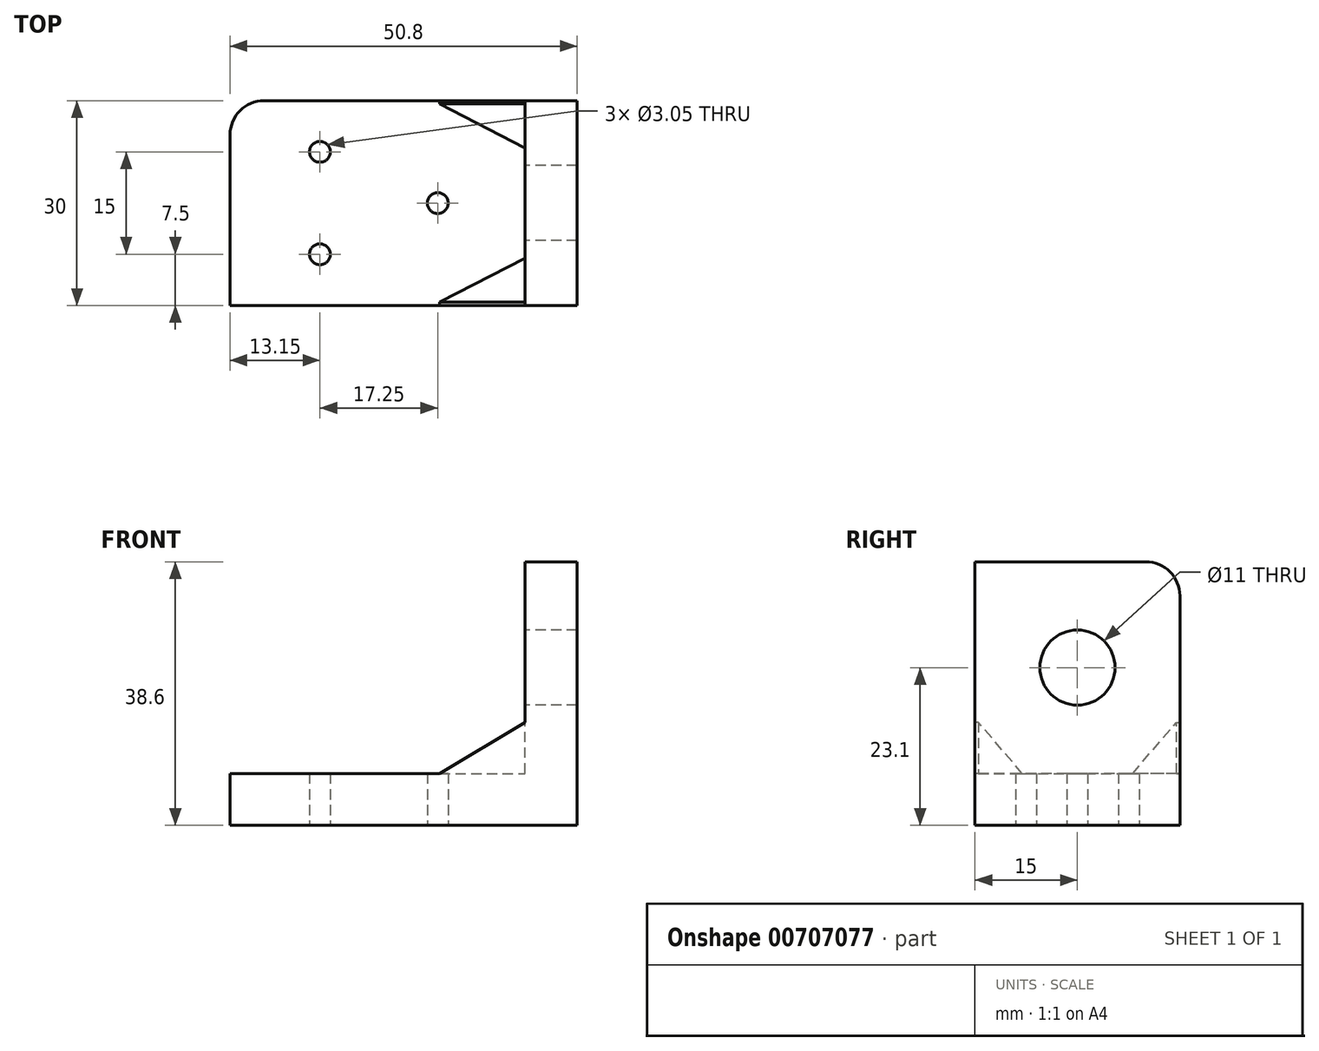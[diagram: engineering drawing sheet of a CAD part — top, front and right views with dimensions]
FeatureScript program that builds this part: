
annotation { "Feature Type Name" : "Feature", "Feature Type Description" : "" }
export const myFeature = defineFeature(function(context is Context, id is Id, definition is map)
    precondition{}
    {
        {
            var Q0;
            Q0=qCreatedBy(makeId("Top.planeOp"),FACE);
            var sketch = newSketch(context, id + "F0", { "sketchPlane" : qUnion([Q0])});
            skLineSegment(sketch, "E0.bottom", {"start": v(25.4, 15) * mm, "end": v(-25.4, 15) * mm});
            skLineSegment(sketch, "E0.top", {"start": v(25.4, -15) * mm, "end": v(-25.4, -15) * mm});
            skLineSegment(sketch, "E0.left", {"start": v(25.4, 15) * mm, "end": v(25.4, -15) * mm});
            skLineSegment(sketch, "E0.right", {"start": v(-25.4, 15) * mm, "end": v(-25.4, -15) * mm});
            skPoint(sketch, "E0.middle", {"position": v(0, 0) * mm});
            skCircle(sketch, "E1", {"center": v(-12.25, 7.5) * mm, "radius": 1.52 * mm});
            skCircle(sketch, "E2", {"center": v(-12.25, -7.5) * mm, "radius": 1.52 * mm});
            skCircle(sketch, "E3", {"center": v(5, 0) * mm, "radius": 1.52 * mm});
            skSolve(sketch);
        }
        {
            var Q0;
            Q0 = qSketchRegion(id + "F0", true);
            extrude(context, id + "F1", {"entities" : qUnion([Q0]), "depth" : 7.6 * mm, "offsetDistance" : 25 * mm});
        }
        {
            var Q0;
            Q0=makeQuery(id+"F1.opExtrude","CAP_FACE",FACE,{"disambiguationData":[OSD([sQuery(id+"F0.wireOp",EDGE,"E0.bottom"),sQuery(id+"F0.wireOp",EDGE,"E0.top"),sQuery(id+"F0.wireOp",EDGE,"E0.left"),sQuery(id+"F0.wireOp",EDGE,"E0.right"),sQuery(id+"F0.wireOp",EDGE,"E1"),sQuery(id+"F0.wireOp",EDGE,"E2"),sQuery(id+"F0.wireOp",EDGE,"E3")])],"isStart":false});
            var sketch = newSketch(context, id + "F2", { "sketchPlane" : qUnion([Q0])});
            skLineSegment(sketch, "E4", {"start": v(25.4, -15) * mm, "end": v(17.8, -15) * mm, "construction": true});
            skLineSegment(sketch, "E5", {"start": v(17.8, -15) * mm, "end": v(17.8, 15) * mm});
            skSolve(sketch);
        }
        {
            var Q0;
            {var subQ0=sQuery(id+"F2.wireOp",EDGE,"E5");Q0=makeQuery(id+"F2.imprint","IMPRINT",FACE,{"disambiguationData":[TD([[makeQuery(id+"F2.imprint","IMPRINT",EDGE,{"derivedFrom":subQ0}),-1.0]])]});}
            extrude(context, id + "F3", {"entities" : qUnion([Q0]), "operationType" : NewBodyOperationType.ADD, "depth" : 31 * mm, "offsetDistance" : 25 * mm});
        }
        {
            var Q0;
            Q0=makeQuery(id+"F3.opExtrude","SWEPT_FACE",FACE,{"disambiguationData":[OSD([sQuery(id+"F2.wireOp",EDGE,"E5")])]});
            var sketch = newSketch(context, id + "F4", { "sketchPlane" : qUnion([Q0])});
            skCircle(sketch, "E6", {"center": v(0, 23.1) * mm, "radius": 5.5 * mm});
            skSolve(sketch);
        }
        {
            var Q0;
            Q0=makeQuery(id+"F4.imprint","IMPRINT",FACE,{"disambiguationData":[TD([[makeQuery(id+"F4.imprint","IMPRINT",EDGE,{"derivedFrom":sQuery(id+"F4.wireOp",EDGE,"E6")}),1.0]])]});
            extrude(context, id + "F5", {"entities" : qUnion([Q0]), "operationType" : NewBodyOperationType.REMOVE, "oppositeDirection" : true, "depth" : 7.6 * mm, "offsetDistance" : 25 * mm});
        }
        {
            var Q0;
            Q0=makeQuery(id+"F3.opExtrude","CAP_EDGE",EDGE,{"disambiguationData":[OSD([sQuery(id+"F0.wireOp",EDGE,"E0.bottom")])],"isStart":false});
            var Q1;
            Q1=makeQuery(id+"F1.opExtrude","SWEPT_EDGE",EDGE,{"disambiguationData":[OSD([sQuery(id+"F0.wireOp",EDGE,"E0.bottom"),sQuery(id+"F0.wireOp",EDGE,"E0.right")])]});
            fillet(context, id + "F6", {"entities" : qUnion([Q0, Q1]), "radius" : 5 * mm, "tangentPropagation" : true, "allowEdgeOverflow" : false});
        }
        {
            var Q0;
            {var subQ0=sQuery(id+"F0.wireOp",EDGE,"E0.bottom");Q0=makeQuery(id+"F3.boolean.opBoolean","MERGE",FACE,{"derivedFrom":[makeQuery(id+"F1.opExtrude","SWEPT_FACE",FACE,{"disambiguationData":[OSD([subQ0])]}),makeQuery(id+"F3.opExtrude","SWEPT_FACE",FACE,{"disambiguationData":[OSD([subQ0])]})]});}
            var sketch = newSketch(context, id + "F7", { "sketchPlane" : qUnion([Q0])});
            skLineSegment(sketch, "E7", {"start": v(-17.8, 15.1) * mm, "end": v(-5.3, 7.6) * mm});
            skSolve(sketch);
        }
        {
            var Q0;
            {var subQ0=sQuery(id+"F0.wireOp",EDGE,"E0.top");Q0=makeQuery(id+"F3.boolean.opBoolean","MERGE",FACE,{"derivedFrom":[makeQuery(id+"F1.opExtrude","SWEPT_FACE",FACE,{"disambiguationData":[OSD([subQ0])]}),makeQuery(id+"F3.opExtrude","SWEPT_FACE",FACE,{"disambiguationData":[OSD([subQ0])]})]});}
            var sketch = newSketch(context, id + "F8", { "sketchPlane" : qUnion([Q0])});
            skLineSegment(sketch, "E8", {"start": v(17.8, 15.1) * mm, "end": v(5.3, 7.6) * mm});
            skSolve(sketch);
        }
        {
            var Q0;
            {var subQ0=sQuery(id+"F7.wireOp",EDGE,"E7");Q0=makeQuery(id+"F7.imprint","IMPRINT",FACE,{"disambiguationData":[TD([[makeQuery(id+"F7.imprint","IMPRINT",EDGE,{"derivedFrom":subQ0}),-1.0]])]});}
            extrude(context, id + "F9", {"entities" : qUnion([Q0]), "operationType" : NewBodyOperationType.ADD, "oppositeDirection" : true, "depth" : 7 * mm, "offsetDistance" : 25 * mm});
        }
        {
            var Q0;
            {var subQ0=sQuery(id+"F8.wireOp",EDGE,"E8");Q0=makeQuery(id+"F8.imprint","IMPRINT",FACE,{"disambiguationData":[TD([[makeQuery(id+"F8.imprint","IMPRINT",EDGE,{"derivedFrom":subQ0}),1.0]])]});}
            extrude(context, id + "F10", {"entities" : qUnion([Q0]), "operationType" : NewBodyOperationType.ADD, "oppositeDirection" : true, "depth" : 7 * mm, "offsetDistance" : 25 * mm});
        }
        {
            var Q0;
            Q0=makeQuery(id+"F9.opExtrude","CAP_EDGE",EDGE,{"disambiguationData":[OSD([sQuery(id+"F7.wireOp",EDGE,"E7")])],"isStart":false});
            var Q1;
            Q1=makeQuery(id+"F10.opExtrude","CAP_EDGE",EDGE,{"disambiguationData":[OSD([sQuery(id+"F8.wireOp",EDGE,"E8")])],"isStart":false});
            chamfer(context, id + "F11", {"entities" : qUnion([Q0, Q1]), "width" : 6.5 * mm, "tangentPropagation" : true});
        }
    });
